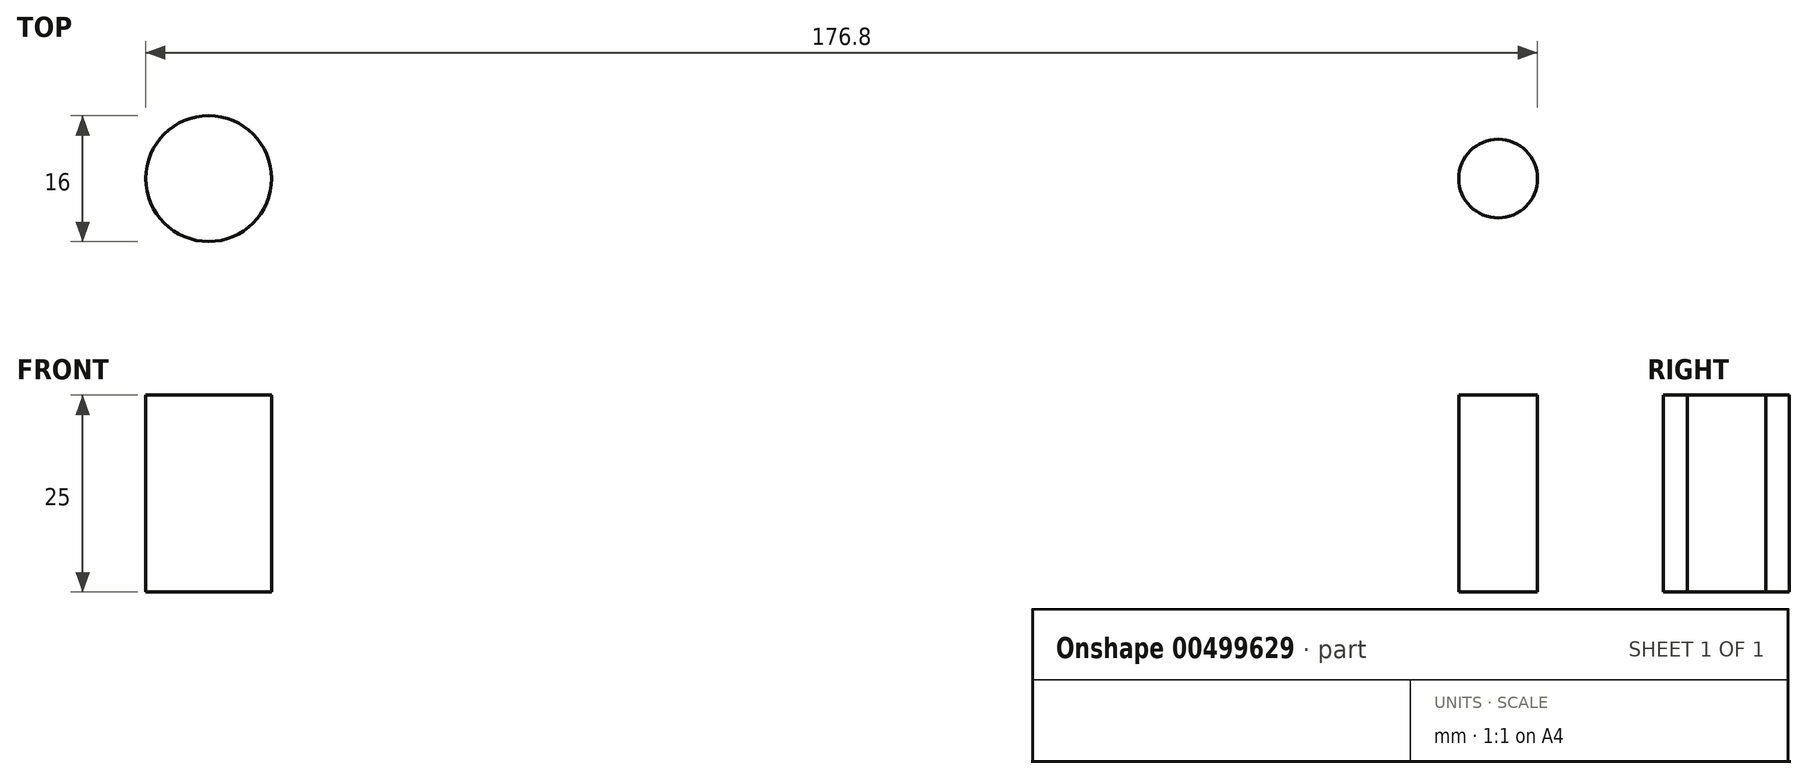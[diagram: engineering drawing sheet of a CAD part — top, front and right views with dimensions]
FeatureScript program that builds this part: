
annotation { "Feature Type Name" : "Feature", "Feature Type Description" : "" }
export const myFeature = defineFeature(function(context is Context, id is Id, definition is map)
    precondition{}
    {
        {
            var Q0;
            Q0=qCreatedBy(makeId("Top.planeOp"),FACE);
            var sketch = newSketch(context, id + "F0", { "sketchPlane" : qUnion([Q0])});
            skCircle(sketch, "E0", {"center": v(0, 0) * mm, "radius": 8 * mm});
            skCircle(sketch, "E1", {"center": v(163.8, 0) * mm, "radius": 5 * mm});
            skSolve(sketch);
        }
        {
            var Q0;
            Q0=qSketchRegion(id+"F0",true);
            extrude(context, id + "F1", {"entities" : qUnion([Q0]), "depth" : 25 * mm, "symmetric" : true});
        }
    });
